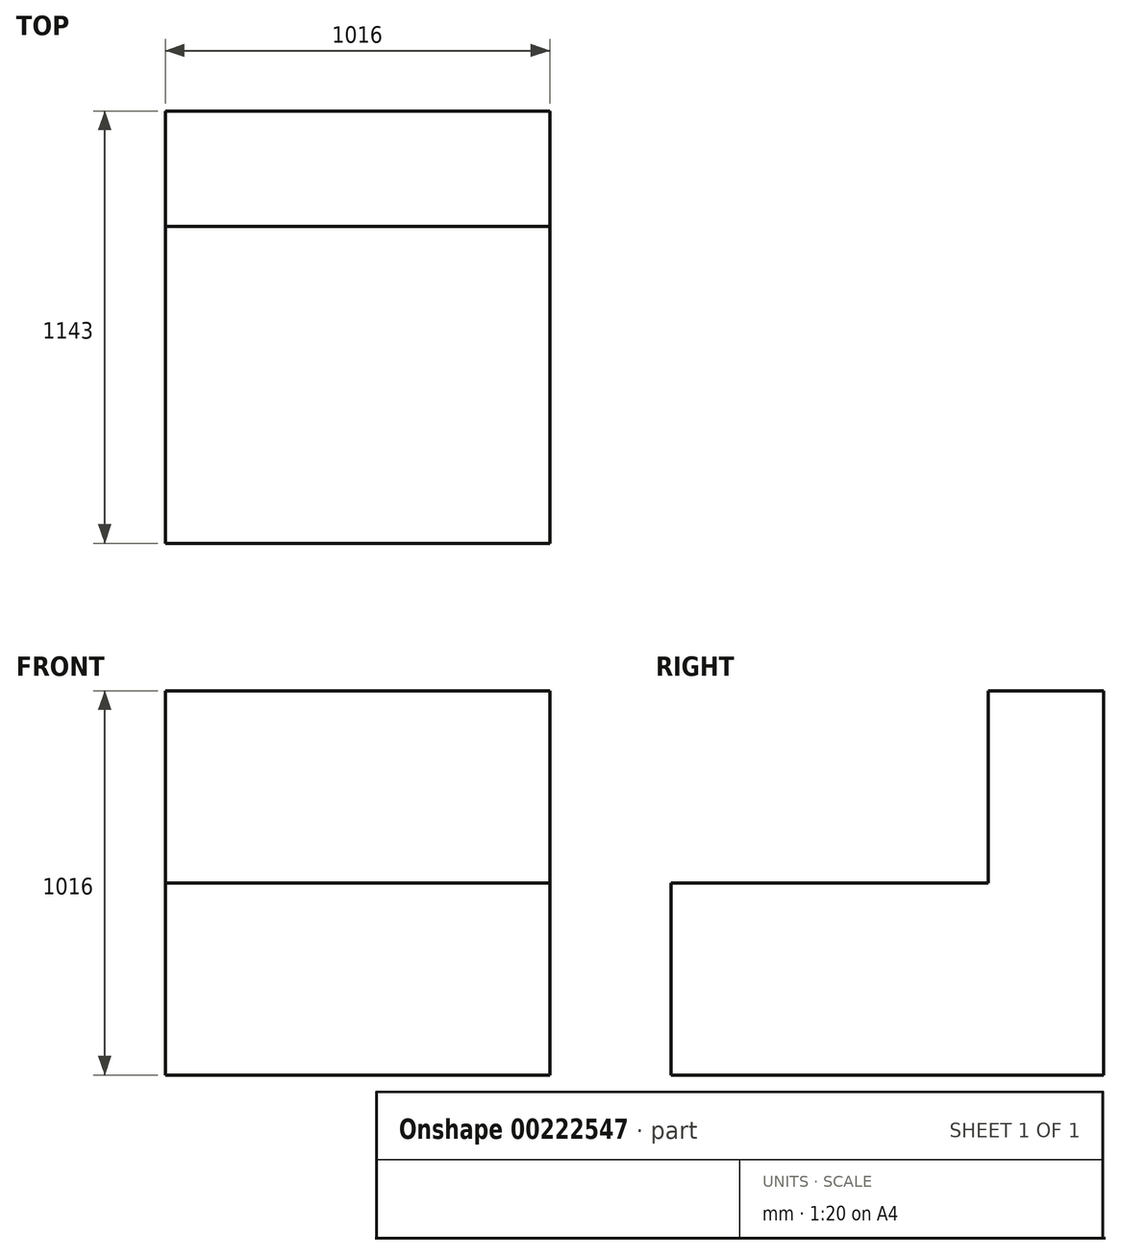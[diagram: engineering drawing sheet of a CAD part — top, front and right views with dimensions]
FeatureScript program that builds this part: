
annotation { "Feature Type Name" : "Feature", "Feature Type Description" : "" }
export const myFeature = defineFeature(function(context is Context, id is Id, definition is map)
    precondition{}
    {
        {
            var Q0;
            Q0=qCreatedBy(makeId("Right.planeOp"),FACE);
            var sketch = newSketch(context, id + "F0", { "sketchPlane" : qUnion([Q0])});
            skLineSegment(sketch, "E0", {"start": v(-787.4, -50.8) * mm, "end": v(-787.4, -558.8) * mm});
            skLineSegment(sketch, "E1", {"start": v(-787.4, -558.8) * mm, "end": v(355.6, -558.8) * mm});
            skLineSegment(sketch, "E2", {"start": v(355.6, -558.8) * mm, "end": v(355.6, 457.2) * mm});
            skLineSegment(sketch, "E3", {"start": v(355.6, 457.2) * mm, "end": v(50.8, 457.2) * mm});
            skLineSegment(sketch, "E4", {"start": v(50.8, 457.2) * mm, "end": v(50.8, -50.8) * mm});
            skLineSegment(sketch, "E5", {"start": v(50.8, -50.8) * mm, "end": v(-787.4, -50.8) * mm});
            skSolve(sketch);
        }
        {
            var Q0;
            Q0 = qSketchRegion(id + "F0", true);
            extrude(context, id + "F1", {"entities" : qUnion([Q0]), "endBound" : BoundingType.SYMMETRIC, "depth" : 1016 * mm});
        }
    });
